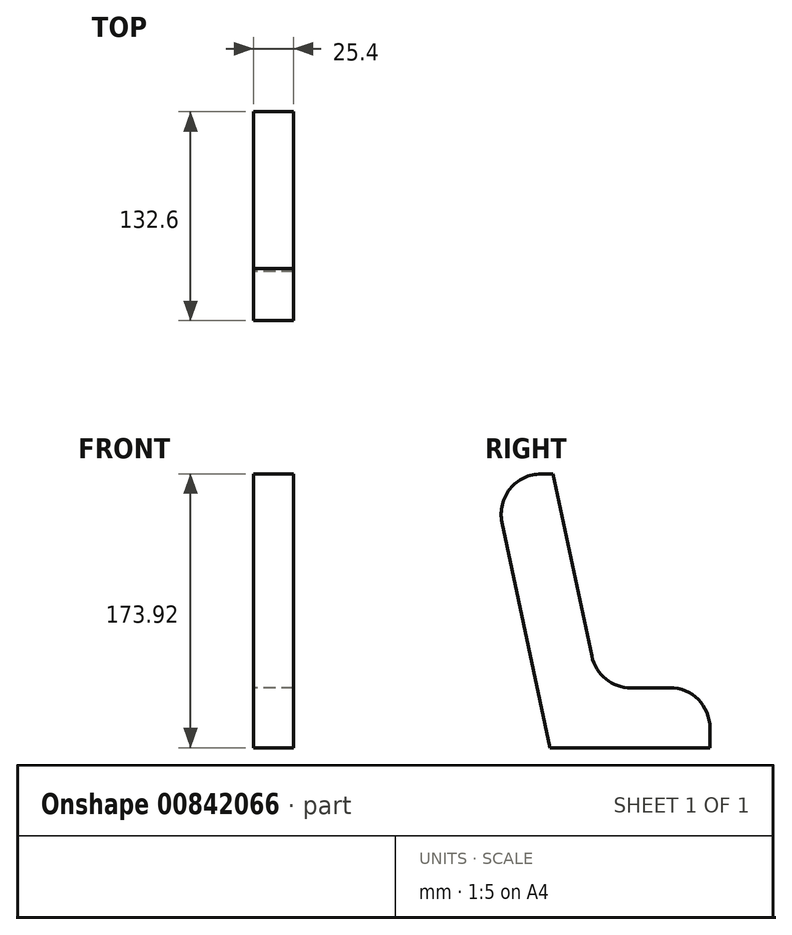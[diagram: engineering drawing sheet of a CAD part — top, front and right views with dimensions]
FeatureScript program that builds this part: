
annotation { "Feature Type Name" : "Feature", "Feature Type Description" : "" }
export const myFeature = defineFeature(function(context is Context, id is Id, definition is map)
    precondition{}
    {
        {
            var Q0;
            Q0=qCreatedBy(makeId("Right.planeOp"),FACE);
            var sketch = newSketch(context, id + "F0", { "sketchPlane" : qUnion([Q0])});
            skLineSegment(sketch, "E0", {"start": v(-35.69, 68.57) * mm, "end": v(-5.24, -74.67) * mm});
            skLineSegment(sketch, "E1", {"start": v(-5.24, -74.67) * mm, "end": v(96.36, -74.67) * mm});
            skLineSegment(sketch, "E2", {"start": v(96.36, -74.67) * mm, "end": v(96.36, -61.97) * mm});
            skLineSegment(sketch, "E3", {"start": v(70.96, -36.57) * mm, "end": v(46.18, -36.57) * mm});
            skLineSegment(sketch, "E4", {"start": v(21.33, -16.45) * mm, "end": v(-3.26, 99.25) * mm});
            skLineSegment(sketch, "E5", {"start": v(-3.26, 99.25) * mm, "end": v(-10.84, 99.25) * mm});
            skArc(sketch, "E6.filletArc", {"start": v(21.33, -16.45) * mm, "mid": v(30.2, -30.9) * mm, "end": v(46.18, -36.57) * mm});
            skPoint(sketch, "E7.visualSharp", {"position": v(96.36, -36.57) * mm});
            skArc(sketch, "E7.filletArc", {"start": v(96.36, -61.97) * mm, "mid": v(88.92, -44) * mm, "end": v(70.96, -36.57) * mm});
            skPoint(sketch, "E8.visualSharp", {"position": v(-42.2, 99.25) * mm});
            skArc(sketch, "E8.filletArc", {"start": v(-10.84, 99.25) * mm, "mid": v(-30.58, 89.83) * mm, "end": v(-35.69, 68.57) * mm});
            skLineSegment(sketch, "E9", {"start": v(-24.01, 13.63) * mm, "end": v(13.26, 21.55) * mm, "construction": true});
            skLineSegment(sketch, "E10", {"start": v(58.57, -36.57) * mm, "end": v(58.57, -74.67) * mm, "construction": true});
            skSolve(sketch);
        }
        {
            var Q0;
            Q0=makeQuery(id+"F0.imprint","IMPRINT",FACE,{"disambiguationData":[TD([[makeQuery(id+"F0.imprint","IMPRINT",EDGE,{"derivedFrom":sQuery(id+"F0.wireOp",EDGE,"E0")}),1.0]])]});
            extrude(context, id + "F1", {"entities" : qUnion([Q0]), "depth" : 25.4 * mm, "offsetDistance" : 25.4 * mm});
        }
    });
